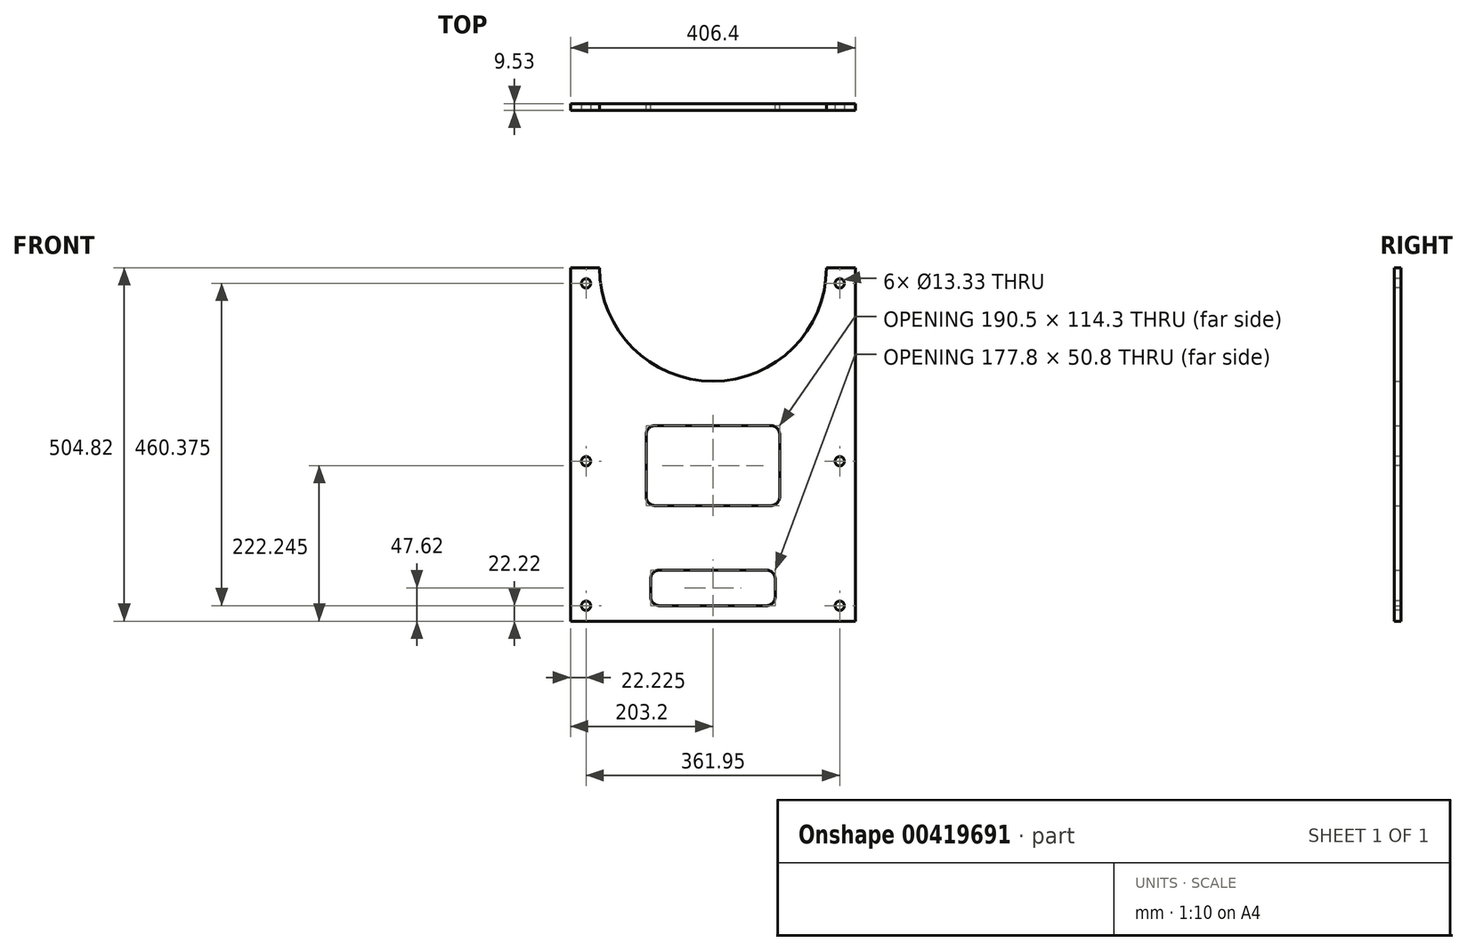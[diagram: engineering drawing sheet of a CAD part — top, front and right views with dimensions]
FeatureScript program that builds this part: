
annotation { "Feature Type Name" : "Feature", "Feature Type Description" : "" }
export const myFeature = defineFeature(function(context is Context, id is Id, definition is map)
    precondition{}
    {
        {
            var Q0;
            Q0=qCreatedBy(makeId("Front.planeOp"),FACE);
            var sketch = newSketch(context, id + "F0", { "sketchPlane" : qUnion([Q0])});
            skArc(sketch, "E0", {"start": v(-161.92, 0) * mm, "mid": v(0, -161.92) * mm, "end": v(161.92, 0) * mm});
            skLineSegment(sketch, "E1", {"start": v(-161.92, 0) * mm, "end": v(-203.2, 0) * mm});
            skLineSegment(sketch, "E2", {"start": v(-203.2, 0) * mm, "end": v(-203.2, -504.83) * mm});
            skLineSegment(sketch, "E3.MirrorCS", {"start": v(161.92, 0) * mm, "end": v(203.2, 0) * mm});
            skLineSegment(sketch, "E4.MirrorCS", {"start": v(203.2, 0) * mm, "end": v(203.2, -504.83) * mm});
            skLineSegment(sketch, "E5", {"start": v(-203.2, -504.83) * mm, "end": v(203.2, -504.83) * mm});
            skLineSegment(sketch, "E6", {"start": v(-95.25, -238.13) * mm, "end": v(-95.25, -327.03) * mm});
            skLineSegment(sketch, "E7", {"start": v(-88.9, -444.5) * mm, "end": v(-88.9, -469.9) * mm});
            skLineSegment(sketch, "E8.MirrorCS", {"start": v(95.25, -238.12) * mm, "end": v(95.25, -327.03) * mm});
            skLineSegment(sketch, "E9.MirrorCS", {"start": v(88.9, -444.5) * mm, "end": v(88.9, -469.9) * mm});
            skLineSegment(sketch, "E10", {"start": v(82.55, -225.43) * mm, "end": v(-82.55, -225.43) * mm});
            skLineSegment(sketch, "E11", {"start": v(-82.55, -339.73) * mm, "end": v(82.55, -339.73) * mm});
            skLineSegment(sketch, "E12", {"start": v(-76.2, -431.8) * mm, "end": v(76.2, -431.8) * mm});
            skLineSegment(sketch, "E13", {"start": v(-76.2, -482.6) * mm, "end": v(76.2, -482.6) * mm});
            skPoint(sketch, "E14.visualSharp", {"position": v(-95.25, -225.43) * mm});
            skArc(sketch, "E14.filletArc", {"start": v(-82.55, -225.43) * mm, "mid": v(-91.53, -229.14) * mm, "end": v(-95.25, -238.13) * mm});
            skPoint(sketch, "E15.visualSharp", {"position": v(95.25, -225.43) * mm});
            skArc(sketch, "E15.filletArc", {"start": v(95.25, -238.12) * mm, "mid": v(91.53, -229.14) * mm, "end": v(82.55, -225.42) * mm});
            skPoint(sketch, "E16.visualSharp", {"position": v(95.25, -339.73) * mm});
            skArc(sketch, "E16.filletArc", {"start": v(82.55, -339.73) * mm, "mid": v(91.53, -336) * mm, "end": v(95.25, -327.03) * mm});
            skPoint(sketch, "E17.visualSharp", {"position": v(-95.25, -339.73) * mm});
            skArc(sketch, "E17.filletArc", {"start": v(-95.25, -327.03) * mm, "mid": v(-91.53, -336) * mm, "end": v(-82.55, -339.73) * mm});
            skPoint(sketch, "E18.visualSharp", {"position": v(-88.9, -431.8) * mm});
            skArc(sketch, "E18.filletArc", {"start": v(-76.2, -431.8) * mm, "mid": v(-85.18, -435.52) * mm, "end": v(-88.9, -444.5) * mm});
            skPoint(sketch, "E19.visualSharp", {"position": v(-88.9, -482.6) * mm});
            skArc(sketch, "E19.filletArc", {"start": v(-88.9, -469.9) * mm, "mid": v(-85.18, -478.88) * mm, "end": v(-76.2, -482.6) * mm});
            skPoint(sketch, "E20.visualSharp", {"position": v(88.9, -482.6) * mm});
            skArc(sketch, "E20.filletArc", {"start": v(76.2, -482.6) * mm, "mid": v(85.18, -478.88) * mm, "end": v(88.9, -469.9) * mm});
            skPoint(sketch, "E21.visualSharp", {"position": v(88.9, -431.8) * mm});
            skArc(sketch, "E21.filletArc", {"start": v(88.9, -444.5) * mm, "mid": v(85.18, -435.52) * mm, "end": v(76.2, -431.8) * mm});
            skSolve(sketch);
        }
        {
            var Q0;
            Q0 = qSketchRegion(id + "F0", true);
            extrude(context, id + "F1", {"entities" : qUnion([Q0]), "depth" : 9.52 * mm});
        }
        {
            var Q0;
            Q0=makeQuery(id+"F1.opExtrude","CAP_FACE",FACE,{"disambiguationData":[OSD([sQuery(id+"F0.wireOp",EDGE,"E0"),sQuery(id+"F0.wireOp",EDGE,"E1"),sQuery(id+"F0.wireOp",EDGE,"E2"),sQuery(id+"F0.wireOp",EDGE,"E3.MirrorCS"),sQuery(id+"F0.wireOp",EDGE,"E4.MirrorCS"),sQuery(id+"F0.wireOp",EDGE,"E5")])],"isStart":false});
            var sketch = newSketch(context, id + "F2", { "sketchPlane" : qUnion([Q0])});
            skCircle(sketch, "E22", {"center": v(-180.97, -482.6) * mm, "radius": 6.67 * mm});
            skCircle(sketch, "E23.MirrorC", {"center": v(180.97, -482.6) * mm, "radius": 6.67 * mm});
            skCircle(sketch, "E24.MirrorC", {"center": v(-180.98, -22.23) * mm, "radius": 6.67 * mm});
            skCircle(sketch, "E25.MirrorC", {"center": v(180.97, -22.22) * mm, "radius": 6.67 * mm});
            skCircle(sketch, "E26.MirrorC", {"center": v(180.97, -276.22) * mm, "radius": 6.67 * mm});
            skCircle(sketch, "E27.MirrorC", {"center": v(-180.97, -276.23) * mm, "radius": 6.67 * mm});
            skSolve(sketch);
        }
        {
            var Q0;
            Q0 = qSketchRegion(id + "F2", true);
            extrude(context, id + "F3", {"entities" : qUnion([Q0]), "operationType" : NewBodyOperationType.REMOVE, "endBound" : BoundingType.THROUGH_ALL, "oppositeDirection" : true, "depth" : 25.4 * mm});
        }
    });
